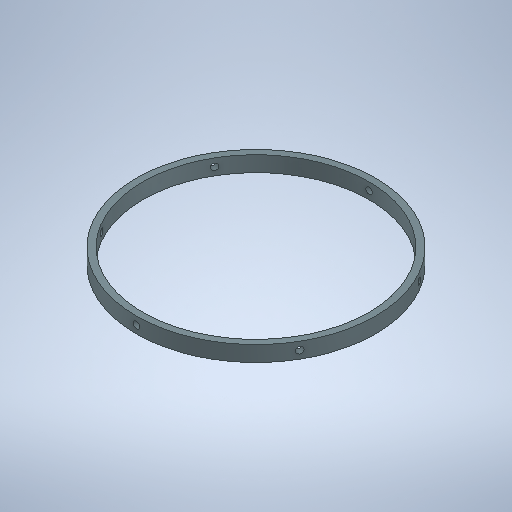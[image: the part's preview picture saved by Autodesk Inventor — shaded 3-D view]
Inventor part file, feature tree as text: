
AUTODESK INVENTOR PART (.ipt)
format: ipt  version: 2025.1 (Build 291241000, 241)  size: 282,112 bytes
history: native  units: mm
features: sketch x2, extrude x1, plane x1, hole x1, pattern_circular x1
ambient origin geometry x8: Origin, YZ Plane, XZ Plane, XY Plane, X Axis, Y Axis, Z Axis, Center Point
bodies: Solid1 (feature_tree)
feature tree (6):
  extrude  "Extrusion1"  Depth=175.0mm
  plane  "Work Plane1"
  hole  "Hole1"  [1 undecoded]
  pattern_circular  "Circular Pattern1"  Count=6 Angle=360.0deg
  sketch  "Sketch1"  dims[d0=185.0mm d1=175.0mm]
  sketch  "Sketch2"  dims[d2=12.0mm d3=0.0mm d4=92.5mm d5=5.0mm d6=6.0mm d7=4.0mm d8=2.0mm d9=90.0deg d10=6.0mm d11=0.0mm d12=60.0mm d13=360.0deg]
note: 1 required parameter value undecoded (feature->parameter linkage not recoverable at this tier; creation-order binding heuristic only, values carry confidence <= 0.55)
